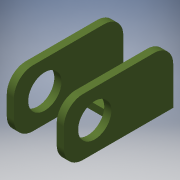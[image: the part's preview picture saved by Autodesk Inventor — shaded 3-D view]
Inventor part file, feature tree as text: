
AUTODESK INVENTOR PART (.ipt)
format: ipt  version: 2017 SP1 (Build 210196100, 196)  size: 162,816 bytes
history: native  units: in
note: dims shown in document units (in); Inventor stores cm internally (conversion verified against a paired STEP export)
features: extrude x3, sketch x3, fillet x1
ambient origin geometry x8: Origin, YZ Plane, XZ Plane, XY Plane, X Axis, Y Axis, Z Axis, Center Point
bodies: Solid1 (feature_tree)
feature tree (7):
  extrude  "Extrusion1"  Depth=1.5in
  extrude  "Extrusion2"  Depth=2.875in TaperAngle=0.0deg
  extrude  "Extrusion3"  Depth=0.75in
  fillet  "Fillet1"  Radius=0.75in
  sketch  "Sketch1"  dims[d0=0.1875in d2=1.5in]
  sketch  "Sketch2"  dims[d3=1.5in d4=2.875in d5=0.0in]
  sketch  "Sketch3"  dims[d6=0.2in d7=0.75in d8=0.75in d10=0.5625in d11=2.5in d12=0.0in d13=0.875in d14=0.75in d15=0.75in d16=1.6875in d17=2.5in d18=0.0in d19=0.5in d21=0.1875in d22=0.1875in]
